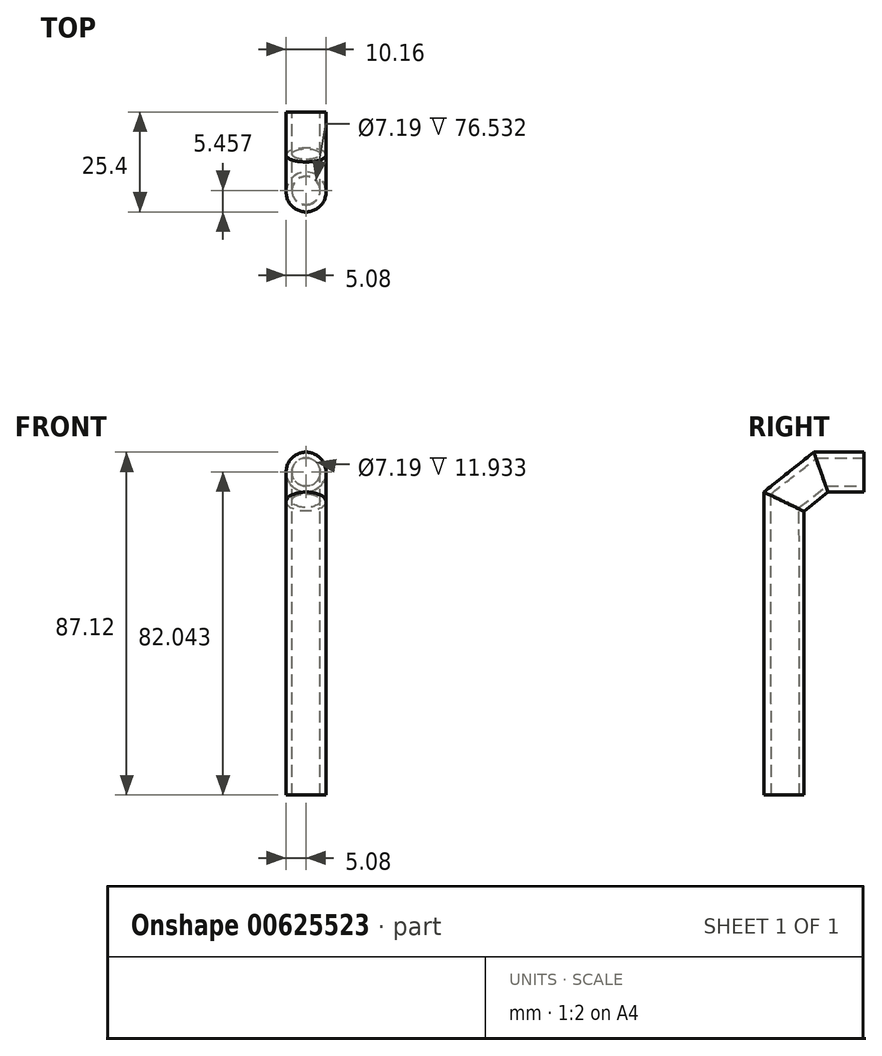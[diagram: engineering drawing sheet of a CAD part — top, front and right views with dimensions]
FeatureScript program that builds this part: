
annotation { "Feature Type Name" : "Feature", "Feature Type Description" : "" }
export const myFeature = defineFeature(function(context is Context, id is Id, definition is map)
    precondition{}
    {
        {
            var Q0;
            Q0=qCreatedBy(makeId("Top.planeOp"),FACE);
            var sketch = newSketch(context, id + "F0", { "sketchPlane" : qUnion([Q0])});
            skCircle(sketch, "E0", {"center": v(0, 0) * mm, "radius": 5.08 * mm});
            skSolve(sketch);
        }
        {
            var Q0;
            Q0=qCreatedBy(makeId("Right.planeOp"),FACE);
            var sketch = newSketch(context, id + "F1", { "sketchPlane" : qUnion([Q0])});
            skLineSegment(sketch, "E1", {"start": v(0, 0) * mm, "end": v(0, 74.51) * mm});
            skLineSegment(sketch, "E2", {"start": v(0, 74.51) * mm, "end": v(9.42, 82.04) * mm});
            skLineSegment(sketch, "E3", {"start": v(9.42, 82.04) * mm, "end": v(20.32, 82.04) * mm});
            skSolve(sketch);
        }
        {
            var Q0;
            Q0=makeQuery(id+"F0.imprint","IMPRINT",FACE,{"disambiguationData":[TD([[makeQuery(id+"F0.imprint","IMPRINT",EDGE,{"derivedFrom":sQuery(id+"F0.wireOp",EDGE,"E0")}),1.0]])]});
            var Q1;
            Q1=sQuery(id+"F1.wireOp",EDGE,"E1");
            var Q2;
            Q2=sQuery(id+"F1.wireOp",EDGE,"E2");
            var Q3;
            Q3=sQuery(id+"F1.wireOp",EDGE,"E3");
            sweep(context, id + "F2", {"profiles" : qUnion([Q0]), "path" : qUnion([Q1, Q2, Q3])});
        }
        {
            var Q0;
            Q0=makeQuery(id+"F2.opSweep","CAP_FACE",FACE,{"disambiguationData":[OSD([sQuery(id+"F0.wireOp",EDGE,"E0"),sQuery(id+"F1.wireOp",VERTEX,"E3.end")])],"isStart":false});
            var sketch = newSketch(context, id + "F3", { "sketchPlane" : qUnion([Q0])});
            skCircle(sketch, "E4", {"center": v(0, 82.04) * mm, "radius": 3.6 * mm});
            skSolve(sketch);
        }
        {
            var Q0;
            Q0=qCreatedBy(makeId("Right.planeOp"),FACE);
            var sketch = newSketch(context, id + "F4", { "sketchPlane" : qUnion([Q0])});
            skLineSegment(sketch, "E5", {"start": v(20.43, 82.35) * mm, "end": v(9.53, 82.35) * mm});
            skLineSegment(sketch, "E6", {"start": v(9.53, 82.35) * mm, "end": v(0, 74.91) * mm});
            skLineSegment(sketch, "E7", {"start": v(0, 74.91) * mm, "end": v(0.15, -0.27) * mm});
            skSolve(sketch);
        }
        {
            var Q0;
            Q0=makeQuery(id+"F3.imprint","IMPRINT",FACE,{"disambiguationData":[TD([[makeQuery(id+"F3.imprint","IMPRINT",EDGE,{"derivedFrom":sQuery(id+"F3.wireOp",EDGE,"E4")}),1.0]])]});
            var Q1;
            Q1=sQuery(id+"F4.wireOp",EDGE,"E5");
            var Q2;
            Q2=sQuery(id+"F4.wireOp",EDGE,"E6");
            var Q3;
            Q3=sQuery(id+"F4.wireOp",EDGE,"E7");
            sweep(context, id + "F5", {"operationType" : NewBodyOperationType.REMOVE, "profiles" : qUnion([Q0]), "path" : qUnion([Q1, Q2, Q3])});
        }
    });
